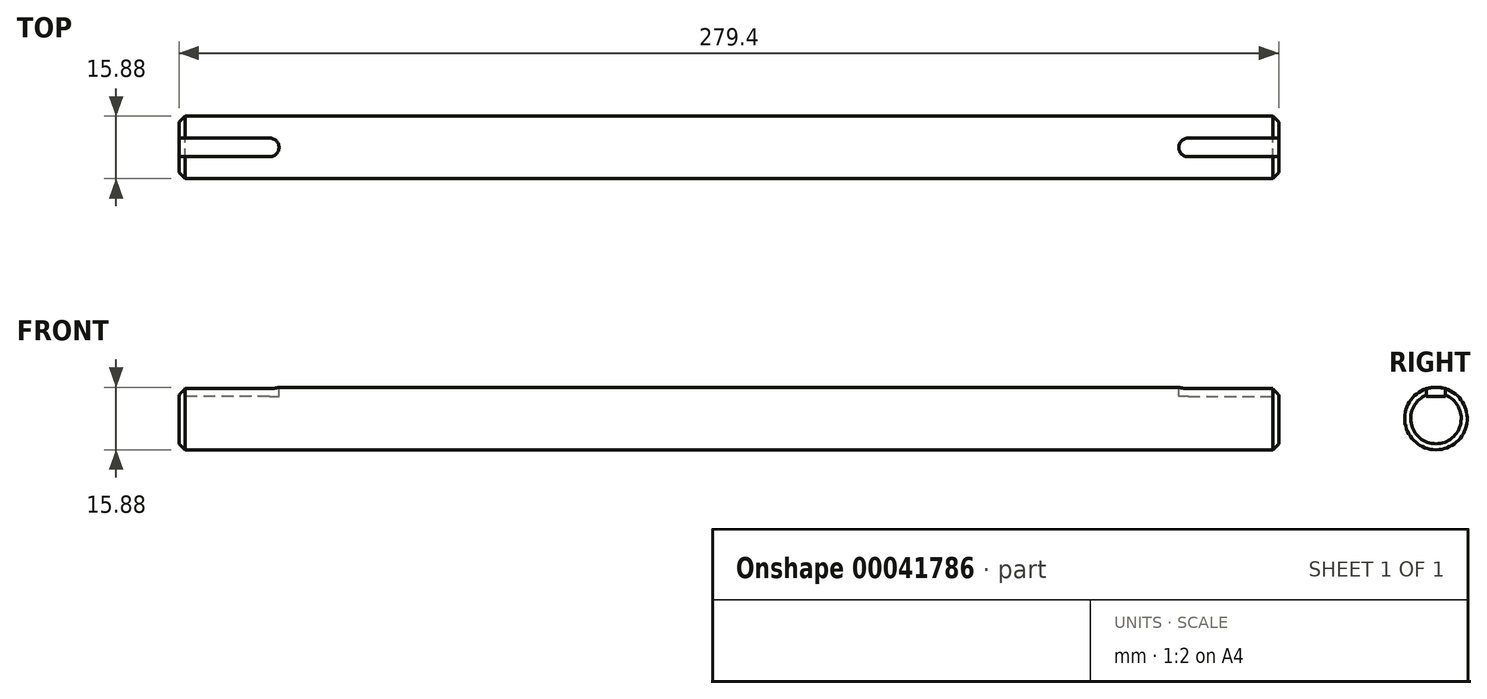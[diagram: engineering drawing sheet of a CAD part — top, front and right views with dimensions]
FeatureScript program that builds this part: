
annotation { "Feature Type Name" : "Feature", "Feature Type Description" : "" }
export const myFeature = defineFeature(function(context is Context, id is Id, definition is map)
    precondition{}
    {
        {
            var Q0;
            Q0=qCreatedBy(makeId("Right.planeOp"),FACE);
            var sketch = newSketch(context, id + "F0", { "sketchPlane" : qUnion([Q0])});
            skCircle(sketch, "E0", {"center": v(0, 0) * mm, "radius": 7.94 * mm});
            skSolve(sketch);
        }
        {
            var Q0;
            Q0 = qSketchRegion(id + "F0", true);
            extrude(context, id + "F1", {"entities" : qUnion([Q0]), "endBound" : BoundingType.SYMMETRIC, "depth" : 279.4 * mm});
        }
        {
            var Q0;
            Q0=qCreatedBy(makeId("Top.planeOp"),FACE);
            cPlane(context, id + "F2", {"entities" : qUnion([Q0]), "cplaneType" : CPlaneType.OFFSET, "offset" : 7.94 * mm, "width" : 152.4 * mm, "height" : 152.4 * mm});
        }
        {
            var Q0;
            Q0=qCreatedBy(id+"F2.planeOp",FACE);
            var sketch = newSketch(context, id + "F3", { "sketchPlane" : qUnion([Q0])});
            skLineSegment(sketch, "E1.0", {"start": v(-139.7, 7.94) * mm, "end": v(-139.7, -7.94) * mm, "construction": true});
            skLineSegment(sketch, "E2.0", {"start": v(139.7, 7.94) * mm, "end": v(139.7, -7.94) * mm, "construction": true});
            skLineSegment(sketch, "E3", {"start": v(-139.7, 0) * mm, "end": v(139.7, 0) * mm, "construction": true});
            skLineSegment(sketch, "E4.0", {"start": v(-116.69, 7.94) * mm, "end": v(-116.69, -7.94) * mm, "construction": true});
            skCircle(sketch, "E5", {"center": v(-116.69, 0) * mm, "radius": 2.38 * mm});
            skLineSegment(sketch, "E6", {"start": v(-116.69, -2.38) * mm, "end": v(-141.9, -2.38) * mm});
            skLineSegment(sketch, "E7", {"start": v(-116.69, 2.38) * mm, "end": v(-143.45, 2.38) * mm});
            skLineSegment(sketch, "E8", {"start": v(-139.7, 2.38) * mm, "end": v(-139.7, -2.38) * mm});
            skLineSegment(sketch, "E9", {"start": v(139.7, -7.94) * mm, "end": v(-139.7, -7.94) * mm, "construction": true});
            skLineSegment(sketch, "E10", {"start": v(0, 29.74) * mm, "end": v(0, -35.72) * mm, "construction": true});
            skPoint(sketch, "E10.startSnap0", {"position": v(0, 0) * mm});
            skCircle(sketch, "E11.MirrorC", {"center": v(116.69, 0) * mm, "radius": 2.38 * mm});
            skLineSegment(sketch, "E12.MirrorCS", {"start": v(139.7, 2.38) * mm, "end": v(139.7, -2.38) * mm});
            skLineSegment(sketch, "E13.MirrorCS", {"start": v(139.7, 7.94) * mm, "end": v(139.7, -7.94) * mm});
            skLineSegment(sketch, "E14.MirrorCS", {"start": v(116.69, 7.94) * mm, "end": v(116.69, -7.94) * mm});
            skLineSegment(sketch, "E15.MirrorCS", {"start": v(116.69, 2.38) * mm, "end": v(143.45, 2.38) * mm});
            skLineSegment(sketch, "E16.MirrorCS", {"start": v(116.69, -2.38) * mm, "end": v(141.9, -2.38) * mm});
            skSolve(sketch);
        }
        {
            var Q0;
            Q0 = qSketchRegion(id + "F3", true);
            extrude(context, id + "F4", {"entities" : qUnion([Q0]), "operationType" : NewBodyOperationType.REMOVE, "oppositeDirection" : true, "depth" : 2.38 * mm});
        }
        {
            var Q0;
            Q0=makeQuery(id+"F1.opExtrude","CAP_EDGE",EDGE,{"disambiguationData":[OSD([sQuery(id+"F0.wireOp",EDGE,"E0")])],"isStart":true});
            var Q1;
            Q1=makeQuery(id+"F1.opExtrude","CAP_EDGE",EDGE,{"disambiguationData":[OSD([sQuery(id+"F0.wireOp",EDGE,"E0")])],"isStart":false});
            chamfer(context, id + "F5", {"entities" : qUnion([Q0, Q1]), "width" : 1.52 * mm, "tangentPropagation" : true});
        }
    });
